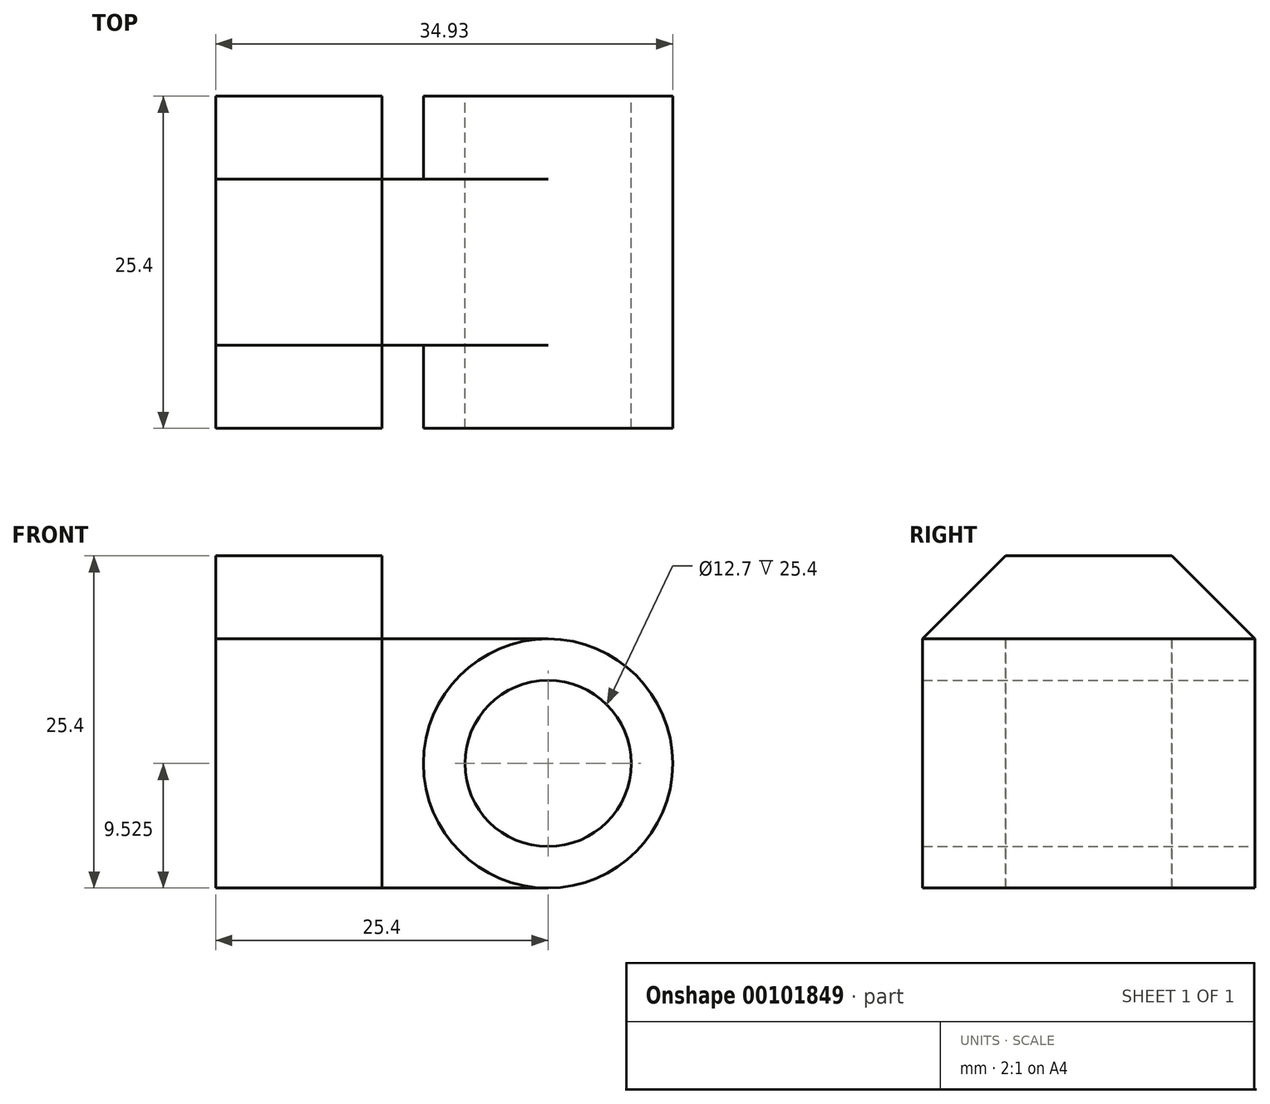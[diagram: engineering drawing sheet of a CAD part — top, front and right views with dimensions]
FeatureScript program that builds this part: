
annotation { "Feature Type Name" : "Feature", "Feature Type Description" : "" }
export const myFeature = defineFeature(function(context is Context, id is Id, definition is map)
    precondition{}
    {
        {
            var Q0;
            Q0=qCreatedBy(makeId("Right.planeOp"),FACE);
            var sketch = newSketch(context, id + "F0", { "sketchPlane" : qUnion([Q0])});
            skLineSegment(sketch, "E0", {"start": v(0, 0) * mm, "end": v(0, 25.4) * mm});
            skLineSegment(sketch, "E1", {"start": v(-25.4, 25.4) * mm, "end": v(-25.4, 0) * mm});
            skLineSegment(sketch, "E2", {"start": v(-25.4, 0) * mm, "end": v(0, 0) * mm});
            skLineSegment(sketch, "E3", {"start": v(-25.4, 25.4) * mm, "end": v(0, 25.4) * mm});
            skSolve(sketch);
        }
        {
            var Q0;
            Q0 = qSketchRegion(id + "F0", true);
            extrude(context, id + "F1", {"entities" : qUnion([Q0]), "oppositeDirection" : true, "depth" : 12.7 * mm});
        }
        {
            var Q0;
            Q0=makeQuery(id+"F1.opExtrude","CAP_FACE",FACE,{"disambiguationData":[OSD([sQuery(id+"F0.wireOp",EDGE,"E0"),sQuery(id+"F0.wireOp",EDGE,"E1"),sQuery(id+"F0.wireOp",EDGE,"E2"),sQuery(id+"F0.wireOp",EDGE,"E3")])],"isStart":false});
            var sketch = newSketch(context, id + "F2", { "sketchPlane" : qUnion([Q0])});
            skLineSegment(sketch, "E4", {"start": v(0, 19.05) * mm, "end": v(6.35, 25.4) * mm});
            skLineSegment(sketch, "E5", {"start": v(25.4, 19.05) * mm, "end": v(19.05, 25.4) * mm});
            skSolve(sketch);
        }
        {
            var Q0;
            {var subQ0=sQuery(id+"F2.wireOp",EDGE,"E4");Q0=makeQuery(id+"F2.imprint","IMPRINT",FACE,{"disambiguationData":[TD([[makeQuery(id+"F2.imprint","IMPRINT",EDGE,{"derivedFrom":subQ0}),1.0]])]});}
            var Q1;
            {var subQ0=sQuery(id+"F2.wireOp",EDGE,"E5");Q1=makeQuery(id+"F2.imprint","IMPRINT",FACE,{"disambiguationData":[TD([[makeQuery(id+"F2.imprint","IMPRINT",EDGE,{"derivedFrom":subQ0}),-1.0]])]});}
            extrude(context, id + "F3", {"entities" : qUnion([Q0, Q1]), "operationType" : NewBodyOperationType.REMOVE, "endBound" : BoundingType.THROUGH_ALL, "oppositeDirection" : true, "depth" : 25.4 * mm});
        }
        {
            var Q0;
            Q0=makeQuery(id+"F1.opExtrude","CAP_FACE",FACE,{"disambiguationData":[OSD([sQuery(id+"F0.wireOp",EDGE,"E0"),sQuery(id+"F0.wireOp",EDGE,"E1"),sQuery(id+"F0.wireOp",EDGE,"E2"),sQuery(id+"F0.wireOp",EDGE,"E3")])],"isStart":true});
            var sketch = newSketch(context, id + "F4", { "sketchPlane" : qUnion([Q0])});
            skLineSegment(sketch, "E6", {"start": v(-19.05, 0) * mm, "end": v(-19.05, 19.05) * mm});
            skLineSegment(sketch, "E7", {"start": v(-19.05, 19.05) * mm, "end": v(-6.35, 19.05) * mm});
            skLineSegment(sketch, "E8", {"start": v(-6.35, 19.05) * mm, "end": v(-6.35, 0) * mm});
            skLineSegment(sketch, "E9", {"start": v(-6.35, 0) * mm, "end": v(-19.05, 0) * mm});
            skSolve(sketch);
        }
        {
            var Q0;
            Q0=makeQuery(id+"F4.imprint","IMPRINT",FACE,{"disambiguationData":[TD([[makeQuery(id+"F4.imprint","IMPRINT",EDGE,{"derivedFrom":sQuery(id+"F4.wireOp",EDGE,"E6")}),-1.0]])]});
            extrude(context, id + "F5", {"entities" : qUnion([Q0]), "operationType" : NewBodyOperationType.ADD, "depth" : 12.7 * mm});
        }
        {
            var Q0;
            Q0=makeQuery(id+"F5.opExtrude","SWEPT_FACE",FACE,{"disambiguationData":[OSD([sQuery(id+"F4.wireOp",EDGE,"E6")])]});
            var sketch = newSketch(context, id + "F6", { "sketchPlane" : qUnion([Q0])});
            skCircle(sketch, "E10", {"center": v(12.7, 9.53) * mm, "radius": 9.53 * mm});
            skCircle(sketch, "E11", {"center": v(12.7, 9.53) * mm, "radius": 6.35 * mm});
            skSolve(sketch);
        }
        {
            var Q0;
            Q0 = qSketchRegion(id + "F6", true);
            var Q1;
            {var subQ1=sQuery(id+"F4.wireOp",EDGE,"E6");var subQ2=makeQuery(id+"F5.opExtrude","CAP_EDGE",EDGE,{"disambiguationData":[OSD([subQ1])],"isStart":false});var subQ5=sQuery(id+"F6.wireOp",EDGE,"E11");var subQ6=makeQuery(id+"F6.imprint","INTERSECT",VERTEX,{"disambiguationData":[OD(0.0)],"derivedFrom":[subQ2,subQ5]});Q1=makeQuery(id+"F6.imprint","IMPRINT",FACE,{"disambiguationData":[TD([[makeQuery(id+"F6.imprint","IMPRINT",EDGE,{"disambiguationData":[TD([[subQ6,-1.0]])],"derivedFrom":subQ5}),-1.0]])]});}
            extrude(context, id + "F7", {"entities" : qUnion([Q0, Q1]), "operationType" : NewBodyOperationType.ADD, "depth" : 6.35 * mm, "hasSecondDirection" : true, "secondDirectionOppositeDirection" : true, "secondDirectionDepth" : 19.05 * mm});
        }
        {
            var Q0;
            {var subQ0=sQuery(id+"F4.wireOp",EDGE,"E6");Q0=makeQuery(id+"F7.boolean.opBoolean","SPLIT",FACE,{"disambiguationData":[TD([makeQuery(id+"F7.opExtrude","SWEPT_FACE",FACE,{"disambiguationData":[OSD([sQuery(id+"F6.wireOp",EDGE,"E11")])]})])],"derivedFrom":makeQuery(id+"F5.opExtrude","SWEPT_FACE",FACE,{"disambiguationData":[OSD([subQ0])]})});}
            extrude(context, id + "F8", {"entities" : qUnion([Q0]), "operationType" : NewBodyOperationType.REMOVE, "endBound" : BoundingType.THROUGH_ALL, "oppositeDirection" : true, "depth" : 25.4 * mm});
        }
    });
